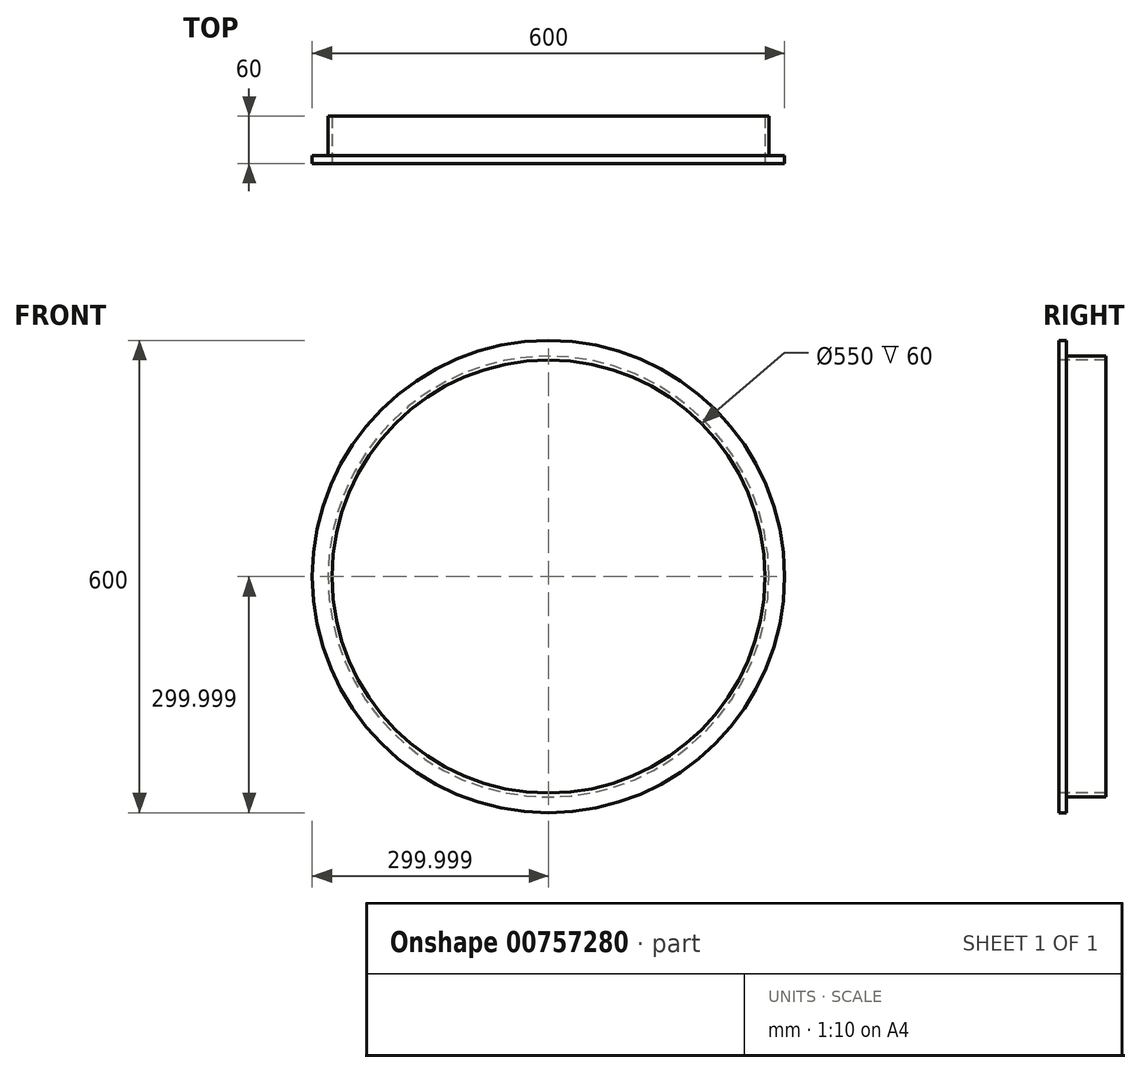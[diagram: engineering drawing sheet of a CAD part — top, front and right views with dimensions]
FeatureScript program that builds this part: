
annotation { "Feature Type Name" : "Feature", "Feature Type Description" : "" }
export const myFeature = defineFeature(function(context is Context, id is Id, definition is map)
    precondition{}
    {
        {
            var Q0;
            Q0=qCreatedBy(makeId("Front.planeOp"),FACE);
            var sketch = newSketch(context, id + "F0", { "sketchPlane" : qUnion([Q0])});
            skCircle(sketch, "E0", {"center": v(0.22, 0.22) * mm, "radius": 275 * mm});
            skCircle(sketch, "E1", {"center": v(0.22, 0.22) * mm, "radius": 300 * mm});
            skCircle(sketch, "E2", {"center": v(0.22, 0.22) * mm, "radius": 280 * mm});
            skSolve(sketch);
        }
        {
            var Q0;
            Q0=makeQuery(id+"F0.imprint","IMPRINT",FACE,{"disambiguationData":[TD([[makeQuery(id+"F0.imprint","IMPRINT",EDGE,{"derivedFrom":sQuery(id+"F0.wireOp",EDGE,"E1")}),1.0]])]});
            extrude(context, id + "F1", {"entities" : qUnion([Q0]), "oppositeDirection" : true, "depth" : 10 * mm, "offsetDistance" : 25 * mm});
        }
        {
            var Q0;
            Q0=makeQuery(id+"F0.imprint","IMPRINT",FACE,{"disambiguationData":[TD([[makeQuery(id+"F0.imprint","IMPRINT",EDGE,{"derivedFrom":sQuery(id+"F0.wireOp",EDGE,"E0")}),-1.0]])]});
            extrude(context, id + "F2", {"entities" : qUnion([Q0]), "operationType" : NewBodyOperationType.ADD, "oppositeDirection" : true, "depth" : 60 * mm, "offsetDistance" : 25 * mm});
        }
    });
